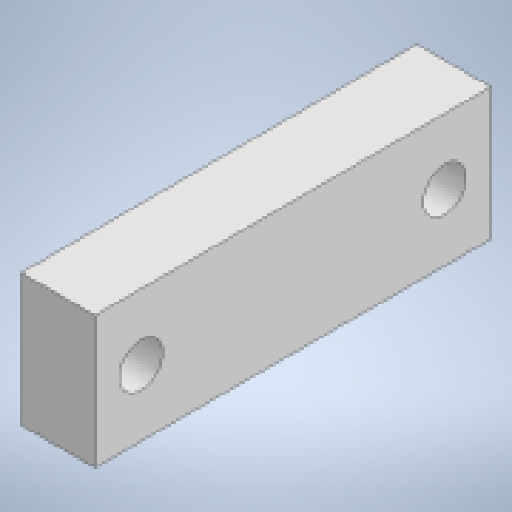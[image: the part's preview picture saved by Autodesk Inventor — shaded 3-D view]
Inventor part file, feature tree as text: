
AUTODESK INVENTOR PART (.ipt)
format: ipt  version: 2023 (Build 270158000, 158)  size: 124,928 bytes
history: native  units: mm
features: extrude x1, sketch x1
ambient origin geometry x8: Origin, YZ Plane, XZ Plane, XY Plane, X Axis, Y Axis, Z Axis, Center Point
bodies: Solid1 (feature_tree)
feature tree (2):
  extrude  "Extrusion1"  Depth=60.0mm
  sketch  "Sketch1"  dims[d0=20.0mm d1=60.0mm d2=6.6mm d3=6.6mm d4=46.0mm d5=10.0mm d6=7.0mm d7=11.2mm d8=0.0mm]
